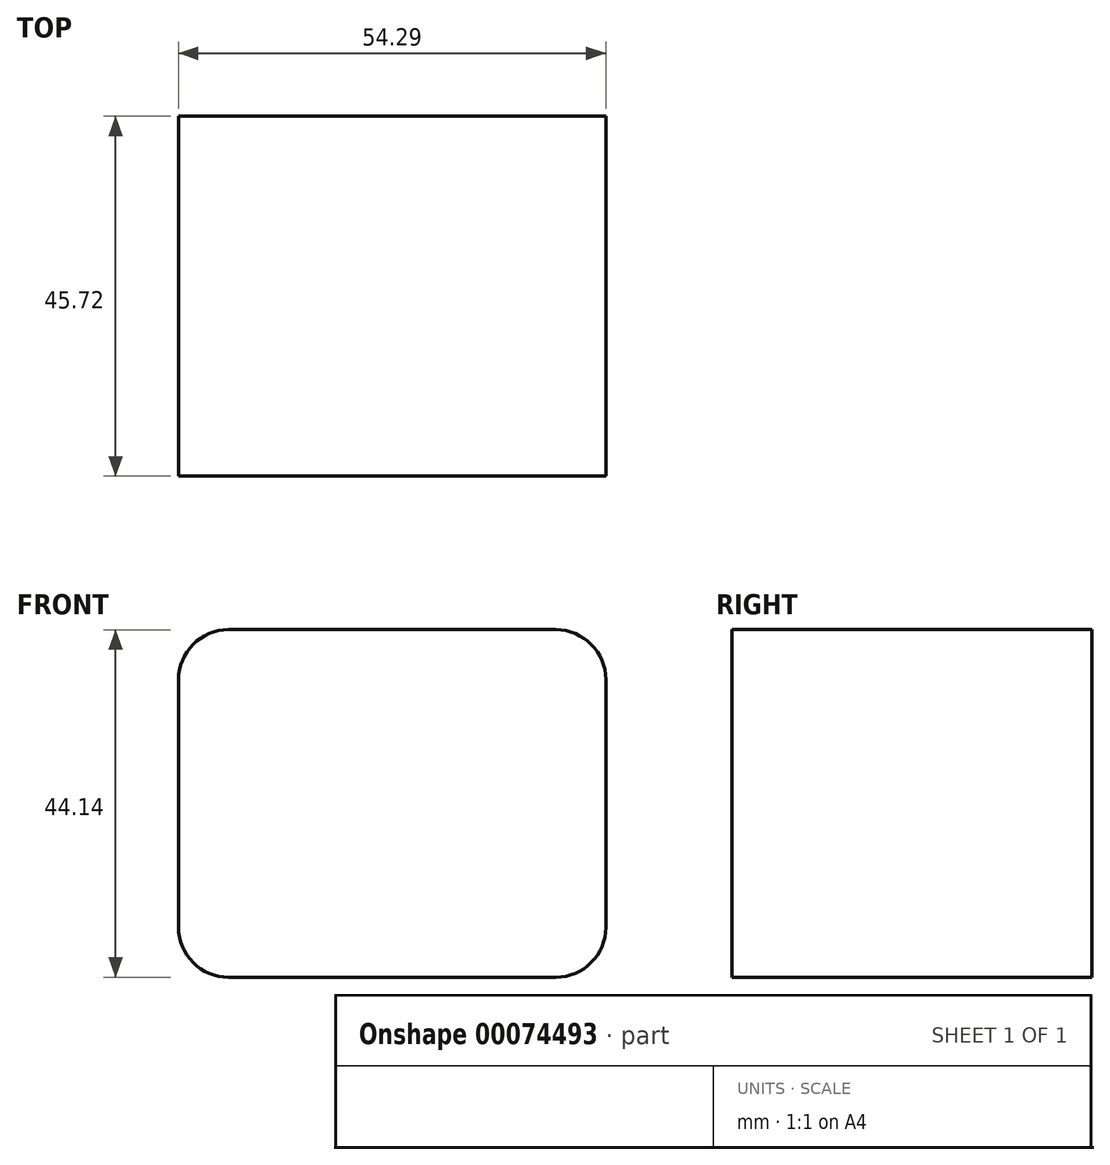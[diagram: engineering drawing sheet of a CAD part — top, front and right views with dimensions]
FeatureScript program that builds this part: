
annotation { "Feature Type Name" : "Feature", "Feature Type Description" : "" }
export const myFeature = defineFeature(function(context is Context, id is Id, definition is map)
    precondition{}
    {
        {
            var Q0;
            Q0=qCreatedBy(makeId("Front.planeOp"),FACE);
            var sketch = newSketch(context, id + "F0", { "sketchPlane" : qUnion([Q0])});
            skLineSegment(sketch, "E0", {"start": v(0, 6.35) * mm, "end": v(0, 37.8) * mm});
            skLineSegment(sketch, "E1", {"start": v(6.35, 44.14) * mm, "end": v(47.94, 44.14) * mm});
            skLineSegment(sketch, "E2", {"start": v(54.3, 37.8) * mm, "end": v(54.3, 6.35) * mm});
            skLineSegment(sketch, "E3", {"start": v(47.94, 0) * mm, "end": v(6.35, 0) * mm});
            skPoint(sketch, "E4.visualSharp", {"position": v(54.3, 44.14) * mm});
            skArc(sketch, "E4.filletArc", {"start": v(54.3, 37.8) * mm, "mid": v(52.43, 42.28) * mm, "end": v(47.94, 44.14) * mm});
            skPoint(sketch, "E5.visualSharp", {"position": v(54.3, 0) * mm});
            skArc(sketch, "E5.filletArc", {"start": v(47.94, 0) * mm, "mid": v(52.43, 1.86) * mm, "end": v(54.3, 6.35) * mm});
            skPoint(sketch, "E6.visualSharp", {"position": v(0, 0) * mm});
            skArc(sketch, "E6.filletArc", {"start": v(0, 6.35) * mm, "mid": v(1.86, 1.86) * mm, "end": v(6.35, 0) * mm});
            skPoint(sketch, "E7.visualSharp", {"position": v(0, 44.14) * mm});
            skArc(sketch, "E7.filletArc", {"start": v(6.35, 44.14) * mm, "mid": v(1.86, 42.28) * mm, "end": v(0, 37.8) * mm});
            skSolve(sketch);
        }
        {
            var Q0;
            Q0=makeQuery(id+"F0.imprint","IMPRINT",FACE,{"disambiguationData":[TD([[makeQuery(id+"F0.imprint","IMPRINT",EDGE,{"derivedFrom":sQuery(id+"F0.wireOp",EDGE,"E0")}),-1.0]])]});
            extrude(context, id + "F1", {"entities" : qUnion([Q0]), "depth" : 45.72 * mm});
        }
    });
